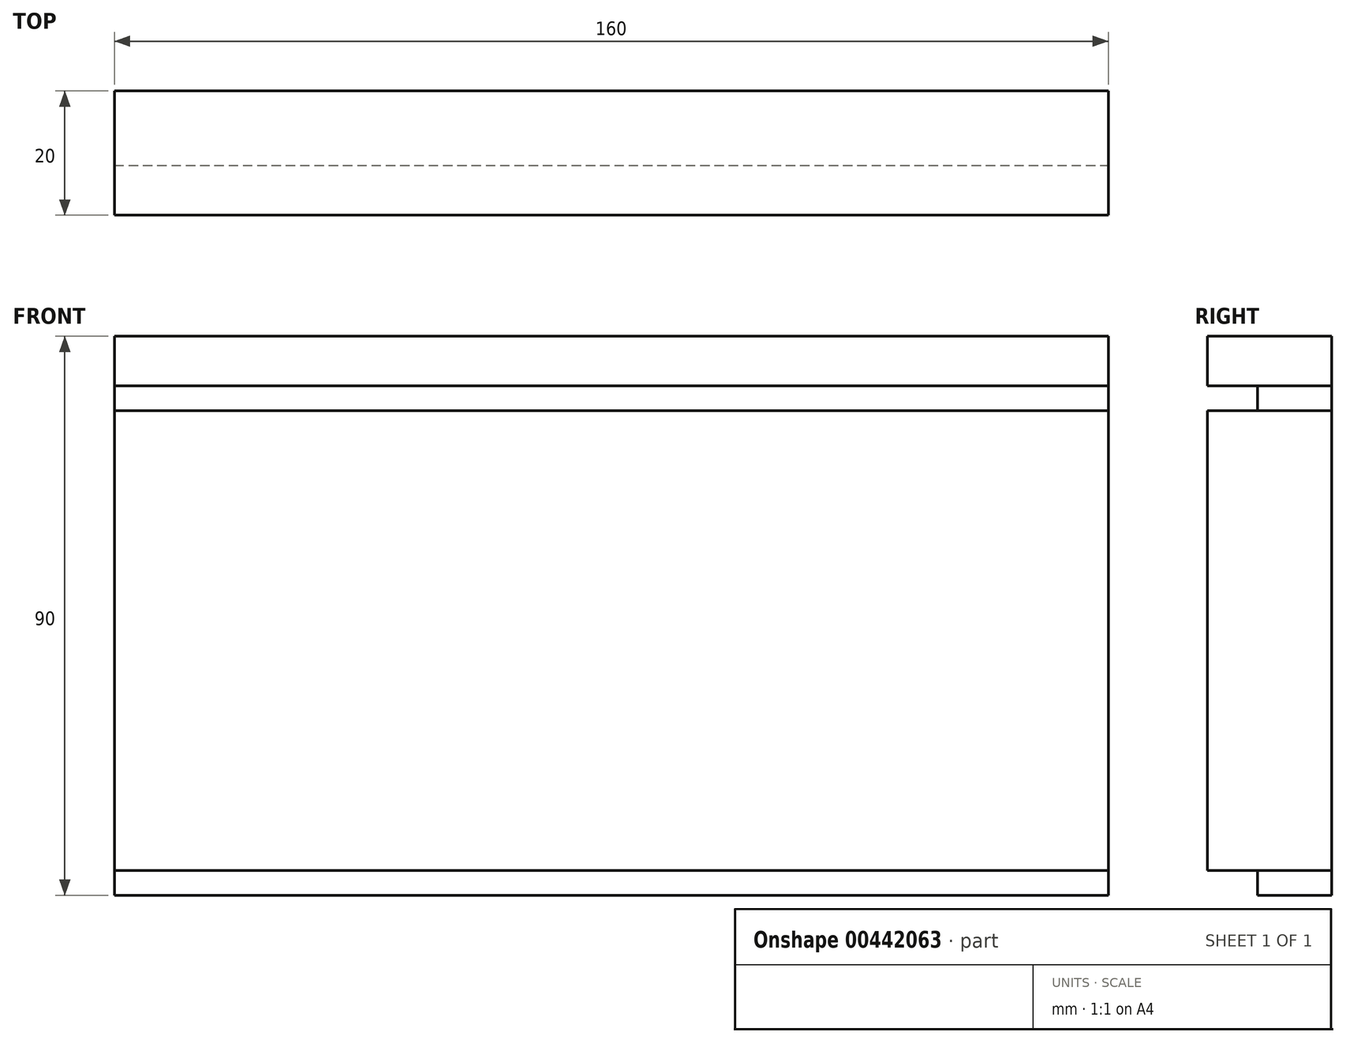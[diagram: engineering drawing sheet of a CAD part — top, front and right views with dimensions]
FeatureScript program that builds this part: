
annotation { "Feature Type Name" : "Feature", "Feature Type Description" : "" }
export const myFeature = defineFeature(function(context is Context, id is Id, definition is map)
    precondition{}
    {
        {
            var Q0;
            Q0=qCreatedBy(makeId("Front.planeOp"),FACE);
            var sketch = newSketch(context, id + "F0", { "sketchPlane" : qUnion([Q0])});
            skLineSegment(sketch, "E0.bottom", {"start": v(80, -45) * mm, "end": v(-80, -45) * mm});
            skLineSegment(sketch, "E0.top", {"start": v(80, 45) * mm, "end": v(-80, 45) * mm});
            skLineSegment(sketch, "E0.left", {"start": v(80, -45) * mm, "end": v(80, 45) * mm});
            skLineSegment(sketch, "E0.right", {"start": v(-80, -45) * mm, "end": v(-80, 45) * mm});
            skPoint(sketch, "E0.middle", {"position": v(0, 0) * mm});
            skLineSegment(sketch, "E1", {"start": v(-80, 37) * mm, "end": v(80, 37) * mm});
            skLineSegment(sketch, "E2", {"start": v(-80, 33) * mm, "end": v(80, 33) * mm});
            skLineSegment(sketch, "E3", {"start": v(-80, -41) * mm, "end": v(80, -41) * mm});
            skSolve(sketch);
        }
        {
            var Q0;
            {var subQ0=sQuery(id+"F0.wireOp",EDGE,"E1");Q0=makeQuery(id+"F0.imprint","IMPRINT",FACE,{"disambiguationData":[TD([[makeQuery(id+"F0.imprint","IMPRINT",EDGE,{"derivedFrom":subQ0}),-1.0]])]});}
            var Q1;
            {var subQ0=sQuery(id+"F0.wireOp",EDGE,"E0.bottom");Q1=makeQuery(id+"F0.imprint","IMPRINT",FACE,{"disambiguationData":[TD([[makeQuery(id+"F0.imprint","IMPRINT",EDGE,{"derivedFrom":subQ0}),-1.0]])]});}
            extrude(context, id + "F1", {"entities" : qUnion([Q0, Q1]), "depth" : 12 * mm});
        }
        {
            var Q0;
            {var subQ0=sQuery(id+"F0.wireOp",EDGE,"E2");Q0=makeQuery(id+"F0.imprint","IMPRINT",FACE,{"disambiguationData":[TD([[makeQuery(id+"F0.imprint","IMPRINT",EDGE,{"derivedFrom":subQ0}),-1.0]])]});}
            var Q1;
            {var subQ0=sQuery(id+"F0.wireOp",EDGE,"E0.top");Q1=makeQuery(id+"F0.imprint","IMPRINT",FACE,{"disambiguationData":[TD([[makeQuery(id+"F0.imprint","IMPRINT",EDGE,{"derivedFrom":subQ0}),1.0]])]});}
            extrude(context, id + "F2", {"entities" : qUnion([Q0, Q1]), "depth" : 20 * mm});
        }
    });
